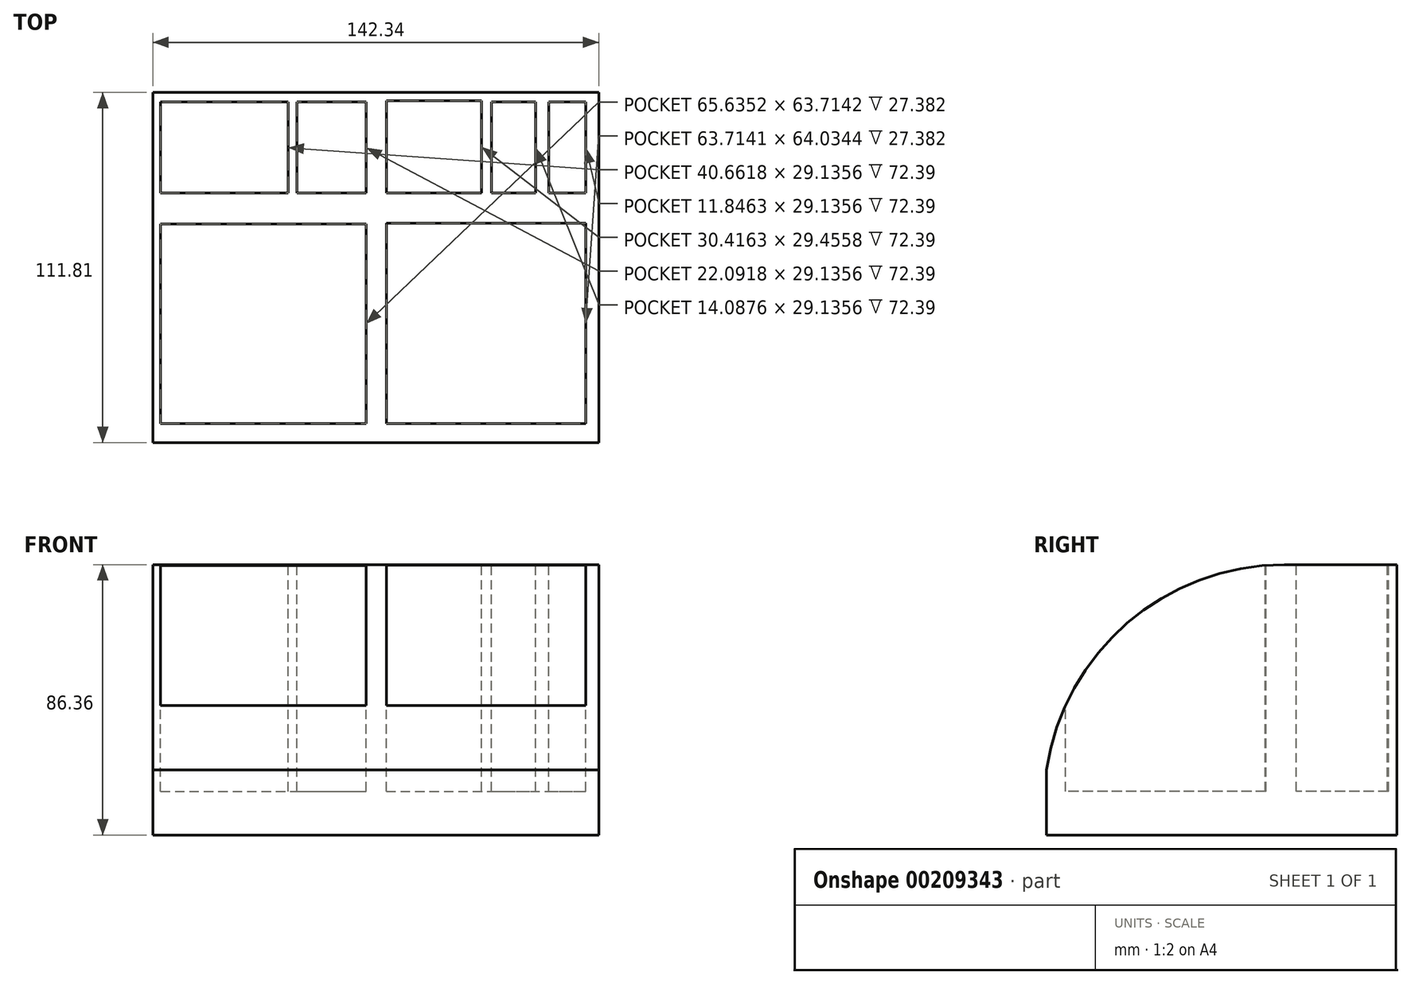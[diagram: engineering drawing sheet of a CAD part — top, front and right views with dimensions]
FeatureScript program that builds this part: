
annotation { "Feature Type Name" : "Feature", "Feature Type Description" : "" }
export const myFeature = defineFeature(function(context is Context, id is Id, definition is map)
    precondition{}
    {
        {
            var Q0;
            Q0=qCreatedBy(makeId("Top.planeOp"),FACE);
            var sketch = newSketch(context, id + "F0", { "sketchPlane" : qUnion([Q0])});
            skLineSegment(sketch, "E0.bottom", {"start": v(-71.6, 56.05) * mm, "end": v(70.74, 56.05) * mm});
            skLineSegment(sketch, "E0.top", {"start": v(-71.6, -55.76) * mm, "end": v(70.74, -55.76) * mm});
            skLineSegment(sketch, "E0.left", {"start": v(-71.6, 56.05) * mm, "end": v(-71.6, -55.76) * mm});
            skLineSegment(sketch, "E0.right", {"start": v(70.74, 56.05) * mm, "end": v(70.74, -55.76) * mm});
            skSolve(sketch);
        }
        {
            var Q0;
            Q0=makeQuery(id+"F0.imprint","IMPRINT",FACE,{"disambiguationData":[TD([[makeQuery(id+"F0.imprint","IMPRINT",EDGE,{"derivedFrom":sQuery(id+"F0.wireOp",EDGE,"E0.bottom")}),-1.0]])]});
            extrude(context, id + "F1", {"entities" : qUnion([Q0]), "depth" : 65.53 * mm});
        }
        {
            var Q0;
            Q0=makeQuery(id+"F1.opExtrude","CAP_EDGE",EDGE,{"disambiguationData":[OSD([sQuery(id+"F0.wireOp",EDGE,"E0.top")])],"isStart":false});
            fillet(context, id + "F2", {"entities" : qUnion([Q0]), "radius" : 76.65 * mm, "tangentPropagation" : true, "allowEdgeOverflow" : false});
        }
        {
            var Q0;
            Q0=makeQuery(id+"F1.opExtrude","CAP_FACE",FACE,{"disambiguationData":[OSD([sQuery(id+"F0.wireOp",EDGE,"E0.bottom"),sQuery(id+"F0.wireOp",EDGE,"E0.top"),sQuery(id+"F0.wireOp",EDGE,"E0.left"),sQuery(id+"F0.wireOp",EDGE,"E0.right")])],"isStart":false});
            var sketch = newSketch(context, id + "F3", { "sketchPlane" : qUnion([Q0])});
            skLineSegment(sketch, "E1.bottom", {"start": v(-69.15, 53.04) * mm, "end": v(-28.48, 53.04) * mm});
            skLineSegment(sketch, "E1.top", {"start": v(-69.15, 23.9) * mm, "end": v(-28.48, 23.9) * mm});
            skLineSegment(sketch, "E1.left", {"start": v(-69.15, 53.04) * mm, "end": v(-69.15, 23.9) * mm});
            skLineSegment(sketch, "E1.right", {"start": v(-28.48, 53.04) * mm, "end": v(-28.48, 23.9) * mm});
            skLineSegment(sketch, "E2.bottom", {"start": v(-25.6, 53.04) * mm, "end": v(-3.5, 53.04) * mm});
            skLineSegment(sketch, "E2.top", {"start": v(-25.6, 23.9) * mm, "end": v(-3.5, 23.9) * mm});
            skLineSegment(sketch, "E2.left", {"start": v(-25.6, 53.04) * mm, "end": v(-25.6, 23.9) * mm});
            skLineSegment(sketch, "E2.right", {"start": v(-3.5, 53.04) * mm, "end": v(-3.5, 23.9) * mm});
            skLineSegment(sketch, "E3.bottom", {"start": v(2.9, 53.36) * mm, "end": v(33.3, 53.36) * mm});
            skLineSegment(sketch, "E3.top", {"start": v(2.9, 23.9) * mm, "end": v(33.3, 23.9) * mm});
            skLineSegment(sketch, "E3.left", {"start": v(2.9, 53.36) * mm, "end": v(2.9, 23.9) * mm});
            skLineSegment(sketch, "E3.right", {"start": v(33.3, 53.36) * mm, "end": v(33.3, 23.9) * mm});
            skLineSegment(sketch, "E4.bottom", {"start": v(36.51, 53.04) * mm, "end": v(50.6, 53.04) * mm});
            skLineSegment(sketch, "E4.top", {"start": v(36.51, 23.9) * mm, "end": v(50.6, 23.9) * mm});
            skLineSegment(sketch, "E4.left", {"start": v(36.51, 53.04) * mm, "end": v(36.51, 23.9) * mm});
            skLineSegment(sketch, "E4.right", {"start": v(50.6, 53.04) * mm, "end": v(50.6, 23.9) * mm});
            skLineSegment(sketch, "E5.bottom", {"start": v(54.76, 53.04) * mm, "end": v(66.6, 53.04) * mm});
            skLineSegment(sketch, "E5.top", {"start": v(54.76, 23.9) * mm, "end": v(66.6, 23.9) * mm});
            skLineSegment(sketch, "E5.left", {"start": v(54.76, 53.04) * mm, "end": v(54.76, 23.9) * mm});
            skLineSegment(sketch, "E5.right", {"start": v(66.6, 53.04) * mm, "end": v(66.6, 23.9) * mm});
            skLineSegment(sketch, "E6.bottom", {"start": v(-69.15, 13.98) * mm, "end": v(-3.5, 13.98) * mm});
            skLineSegment(sketch, "E6.top", {"start": v(-69.15, -49.74) * mm, "end": v(-3.5, -49.74) * mm});
            skLineSegment(sketch, "E6.left", {"start": v(-69.15, 13.98) * mm, "end": v(-69.15, -49.74) * mm});
            skLineSegment(sketch, "E6.right", {"start": v(-3.5, 13.98) * mm, "end": v(-3.5, -49.74) * mm});
            skLineSegment(sketch, "E7.bottom", {"start": v(2.9, 14.3) * mm, "end": v(66.6, 14.3) * mm});
            skLineSegment(sketch, "E7.top", {"start": v(2.9, -49.74) * mm, "end": v(66.6, -49.74) * mm});
            skLineSegment(sketch, "E7.left", {"start": v(2.9, 14.3) * mm, "end": v(2.9, -49.74) * mm});
            skLineSegment(sketch, "E7.right", {"start": v(66.6, 14.3) * mm, "end": v(66.6, -49.74) * mm});
            skSolve(sketch);
        }
        {
            var Q0;
            Q0=makeQuery(id+"F1.opExtrude","CAP_FACE",FACE,{"disambiguationData":[OSD([sQuery(id+"F0.wireOp",EDGE,"E0.bottom"),sQuery(id+"F0.wireOp",EDGE,"E0.top"),sQuery(id+"F0.wireOp",EDGE,"E0.left"),sQuery(id+"F0.wireOp",EDGE,"E0.right")])],"isStart":true});
            extrude(context, id + "F4", {"entities" : qUnion([Q0]), "operationType" : NewBodyOperationType.ADD, "depth" : 20.83 * mm});
        }
        {
            var Q0;
            Q0=makeQuery(id+"F3.imprint","IMPRINT",FACE,{"disambiguationData":[TD([[makeQuery(id+"F3.imprint","IMPRINT",EDGE,{"derivedFrom":sQuery(id+"F3.wireOp",EDGE,"E6.bottom")}),-1.0]])]});
            var Q1;
            Q1=makeQuery(id+"F3.imprint","IMPRINT",FACE,{"disambiguationData":[TD([[makeQuery(id+"F3.imprint","IMPRINT",EDGE,{"derivedFrom":sQuery(id+"F3.wireOp",EDGE,"E7.bottom")}),-1.0]])]});
            var Q2;
            Q2=makeQuery(id+"F3.imprint","IMPRINT",FACE,{"disambiguationData":[TD([[makeQuery(id+"F3.imprint","IMPRINT",EDGE,{"derivedFrom":sQuery(id+"F3.wireOp",EDGE,"E3.bottom")}),-1.0]])]});
            var Q3;
            Q3=makeQuery(id+"F3.imprint","IMPRINT",FACE,{"disambiguationData":[TD([[makeQuery(id+"F3.imprint","IMPRINT",EDGE,{"derivedFrom":sQuery(id+"F3.wireOp",EDGE,"E2.bottom")}),-1.0]])]});
            var Q4;
            Q4=makeQuery(id+"F3.imprint","IMPRINT",FACE,{"disambiguationData":[TD([[makeQuery(id+"F3.imprint","IMPRINT",EDGE,{"derivedFrom":sQuery(id+"F3.wireOp",EDGE,"E4.bottom")}),-1.0]])]});
            var Q5;
            Q5=makeQuery(id+"F3.imprint","IMPRINT",FACE,{"disambiguationData":[TD([[makeQuery(id+"F3.imprint","IMPRINT",EDGE,{"derivedFrom":sQuery(id+"F3.wireOp",EDGE,"E5.bottom")}),-1.0]])]});
            var Q6;
            Q6=makeQuery(id+"F3.imprint","IMPRINT",FACE,{"disambiguationData":[TD([[makeQuery(id+"F3.imprint","IMPRINT",EDGE,{"derivedFrom":sQuery(id+"F3.wireOp",EDGE,"E1.bottom")}),-1.0]])]});
            extrude(context, id + "F5", {"entities" : qUnion([Q0, Q1, Q2, Q3, Q4, Q5, Q6]), "operationType" : NewBodyOperationType.REMOVE, "oppositeDirection" : true, "depth" : 72.39 * mm});
        }
    });
